# Revit family: Casement_38_A_Side_Hung_Custom
name_source: partatom
category: Windows
revit_build: Autodesk Revit 2014 (Build: 20130308_1515(x64)
units: mm (PartAtom-declared; Revit-internal decimal feet)

## types (1)
- 38-TypeA-SideHung-Custom
    Aluminium Thickness = 1 mm  [stored 0.00328084 ft]
    Bead SG Gap = 13 mm  [stored 0.0426509 ft]
    Casement Dimension = 38 mm  [stored 0.124672 ft]
    Custom Windload = 1000 mm  [stored 3.28084 ft]
    Custom Window Exterior Offset = 81 mm  [stored 0.265748 ft]
    Custom Window Height = 900 mm  [stored 2.95276 ft]
    Custom Window Width = 600 mm  [stored 1.9685 ft]
    DG Extrusion Start = 9 mm  [stored 0.0295276 ft]
    DG Gasket Finish = Double Glazing Gasket Material
    DG Thickness Calc = 4 mm  [stored 0.0131234 ft]
    Default Sill Height = 800 mm  [stored 2.62467 ft]
    Depth Bead = 24 mm  [stored 0.0787402 ft]
    Description = Window 38mm, Type A side hung custom
    Frame Center Offset = 19 mm  [stored 0.062336 ft]
    Height = 900 mm  [stored 2.95276 ft]
    Height Sash = 824 mm  [stored 2.70341 ft]
    Height Sash 1 Opening = 854 mm
    Limit Sash Height Max = 1500 mm  [stored 4.92126 ft]
    Limit Sash Height Min = 300 mm  [stored 0.984252 ft]
    Limit Sash Width Max = 700 mm  [stored 2.29659 ft]
    Limit Sash Width Min = 300 mm  [stored 0.984252 ft]
    Limit Window Height Max = 1546 mm  [stored 5.07218 ft]
    Limit Window Height Min = 346 mm
    Limit Window Width Max = 746 mm  [stored 2.44751 ft]
    Limit Window Width Min = 346 mm
    Manufacturer = Crealco
    Max Pane Area = 0.38 m²
    Max System DG One Piece Thickness = 6 mm  [stored 0.019685 ft]
    Max System DG Unit Thickness = 25 mm  [stored 0.082021 ft]
    Model = Casement 38
    Offset Bead SG Center Reversed = 19 mm  [stored 0.062336 ft]
    Offset Sash 1 Top = 23 mm  [stored 0.0754593 ft]
    Offset Sash Left = 23 mm  [stored 0.0754593 ft]
    Offset Window Exterior = 100 mm  [stored 0.328084 ft]
    SG Gasket Thickness = 6 mm  [stored 0.019685 ft]
    Sash Center Offset = 16 mm  [stored 0.0524934 ft]
    Sash Height = 854 mm
    Sash Overlap = 7 mm  [stored 0.0229659 ft]
    Sash Spacing Inner = 8 mm  [stored 0.0262467 ft]
    Sash Width = 554 mm  [stored 1.81759 ft]
    URL = http://www.crealco.co.za
    Wall Closure = By host
    Width = 600 mm  [stored 1.9685 ft]
    Width Bead = 15 mm  [stored 0.0492126 ft]
    Width Profile = 30 mm  [stored 0.0984252 ft]
    Width Sash = 524 mm  [stored 1.71916 ft]
    Width Sash Opening = 554 mm  [stored 1.81759 ft]
    Windload Design = 1000 mm  [stored 3.28084 ft]

note: [stored X ft] marks values corroborated as IEEE doubles in the binary element streams (Revit-internal decimal feet)

## geometry (parser evidence)
native form markers: Extrusion x1, Sweep x31
no freeform markers — native parametric forms only
